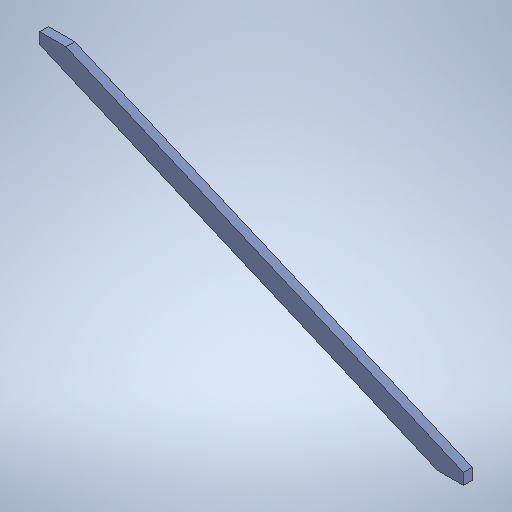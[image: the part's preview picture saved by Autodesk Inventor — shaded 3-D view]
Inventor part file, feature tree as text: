
AUTODESK INVENTOR PART (.ipt)
format: ipt  version: 2025.1 (Build 291241020, 241B)  size: 250,368 bytes
history: native  units: in
note: dims shown in document units (in); Inventor stores cm internally (conversion verified against a paired STEP export)
features: other x7, reference x4, extrude x1, sketch x1
ambient origin geometry x8: Origin, YZ Plane, XZ Plane, XY Plane, X Axis, Y Axis, Z Axis, Center Point
bodies: Solid1 (feature_tree)
feature tree (13):
  extrude  "Extrusion1"  [1 undecoded]
  sketch  "Sketch1"  dims[d2=1.5in d3=0.0in]
  reference  "Reference1"
  reference  "Reference2"
  reference  "Reference3"
  reference  "Reference4"
  other  "<userpath>\Documents\Tburn24\Assembly1.iam"
  other  "Assembly1.iam"
  other  "16'x2x4:1"
  other  "6'x4x4:19"
  other  "16'x4x4:2"
  other  "6'x4x4:15"
  other  "Finish1"
note: 1 required parameter value undecoded (feature->parameter linkage not recoverable at this tier; creation-order binding heuristic only, values carry confidence <= 0.55)
